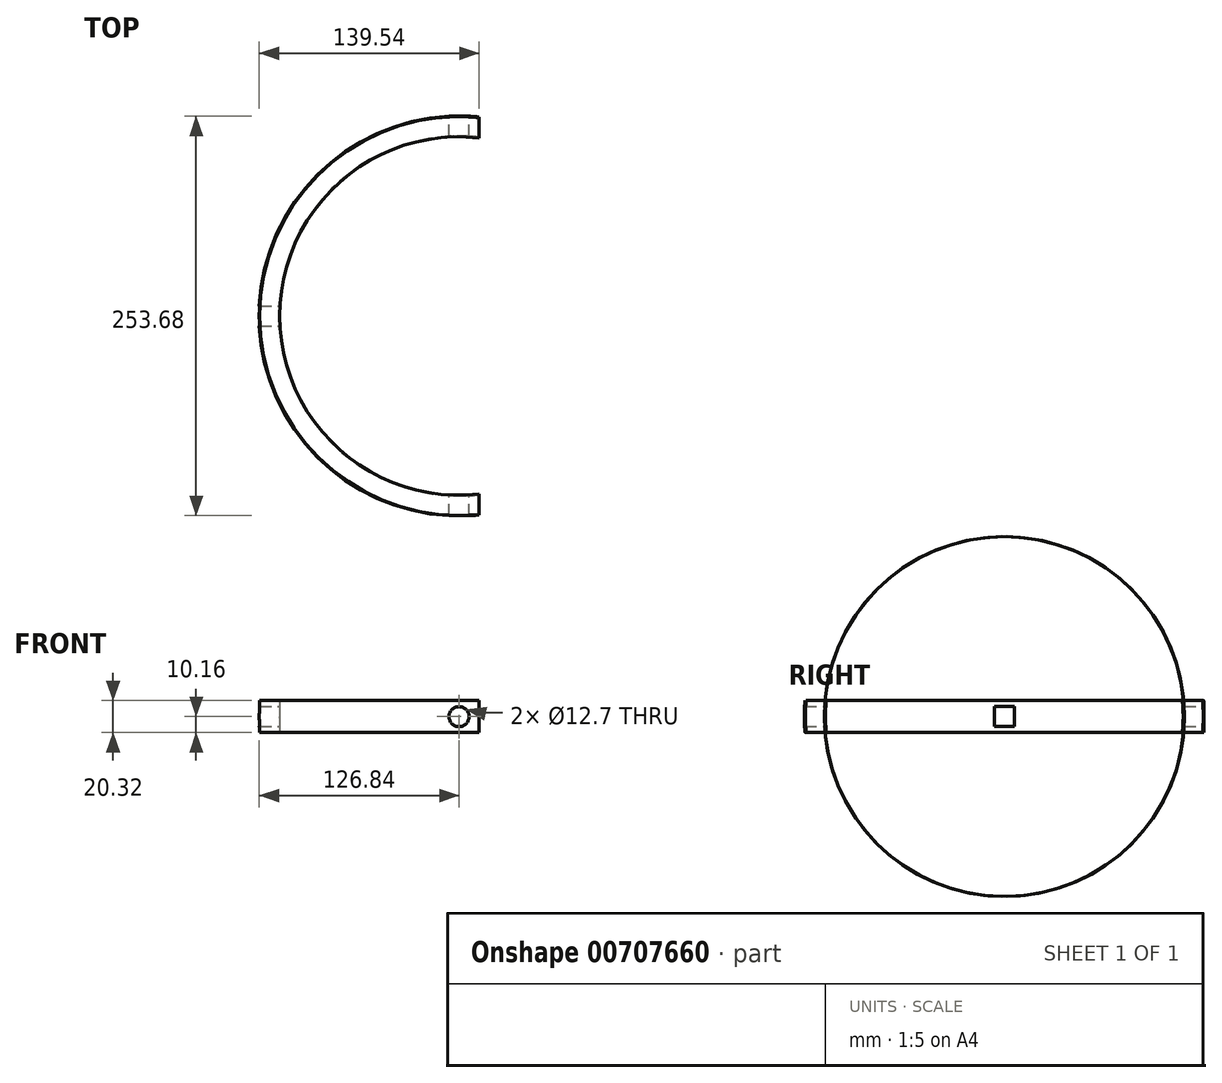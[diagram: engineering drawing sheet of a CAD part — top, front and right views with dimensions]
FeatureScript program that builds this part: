
annotation { "Feature Type Name" : "Feature", "Feature Type Description" : "" }
export const myFeature = defineFeature(function(context is Context, id is Id, definition is map)
    precondition{}
    {
        {
            var Q0;
            Q0=qCreatedBy(makeId("Top.planeOp"),FACE);
            var sketch = newSketch(context, id + "F0", { "sketchPlane" : qUnion([Q0])});
            skArc(sketch, "E0", {"start": v(12.7, 126.36) * mm, "mid": v(-85.2, 94.19) * mm, "end": v(-127, 0) * mm});
            skArc(sketch, "E1", {"start": v(12.7, 113.6) * mm, "mid": v(-76.2, 85.2) * mm, "end": v(-114.3, 0) * mm});
            skLineSegment(sketch, "E2", {"start": v(12.7, 126.36) * mm, "end": v(12.7, 113.6) * mm});
            skLineSegment(sketch, "E3", {"start": v(-127, 0) * mm, "end": v(-114.3, 0) * mm});
            skLineSegment(sketch, "E4", {"start": v(-86.87, 0) * mm, "end": v(85.39, 0) * mm, "construction": true});
            skSolve(sketch);
        }
        {
            var Q0;
            Q0 = qSketchRegion(id + "F0", true);
            var Q1;
            Q1=sQuery(id+"F0.wireOp",EDGE,"E4");
            revolve(context, id + "F1", {"surfaceOperationType" : NewSurfaceOperationType.NEW, "entities" : qUnion([Q0]), "axis" : qUnion([Q1]), "revolveType" : RevolveType.FULL});
        }
        {
            var Q0;
            Q0=qCreatedBy(makeId("Right.planeOp"),FACE);
            var sketch = newSketch(context, id + "F2", { "sketchPlane" : qUnion([Q0])});
            skLineSegment(sketch, "E5.bottom", {"start": v(-6.35, 6.35) * mm, "end": v(6.35, 6.35) * mm});
            skLineSegment(sketch, "E5.top", {"start": v(-6.35, -6.35) * mm, "end": v(6.35, -6.35) * mm});
            skLineSegment(sketch, "E5.left", {"start": v(-6.35, 6.35) * mm, "end": v(-6.35, -6.35) * mm});
            skLineSegment(sketch, "E5.right", {"start": v(6.35, 6.35) * mm, "end": v(6.35, -6.35) * mm});
            skLineSegment(sketch, "E6.bottom", {"start": v(-169.08, 138.73) * mm, "end": v(200.28, 138.73) * mm});
            skLineSegment(sketch, "E6.top", {"start": v(-169.08, 10.16) * mm, "end": v(200.28, 10.16) * mm});
            skLineSegment(sketch, "E6.left", {"start": v(-169.08, 138.73) * mm, "end": v(-169.08, 10.16) * mm});
            skLineSegment(sketch, "E6.right", {"start": v(200.28, 138.73) * mm, "end": v(200.28, 10.16) * mm});
            skLineSegment(sketch, "E7.bottom", {"start": v(-163.02, -10.16) * mm, "end": v(196.26, -10.16) * mm});
            skLineSegment(sketch, "E7.top", {"start": v(-163.02, -153.36) * mm, "end": v(196.26, -153.36) * mm});
            skLineSegment(sketch, "E7.left", {"start": v(-163.02, -10.16) * mm, "end": v(-163.02, -153.36) * mm});
            skLineSegment(sketch, "E7.right", {"start": v(196.26, -10.16) * mm, "end": v(196.26, -153.36) * mm});
            skSolve(sketch);
        }
        {
            var Q0;
            Q0=makeQuery(id+"F2.imprint","IMPRINT",FACE,{"disambiguationData":[TD([[makeQuery(id+"F2.imprint","IMPRINT",EDGE,{"derivedFrom":sQuery(id+"F2.wireOp",EDGE,"E6.bottom")}),-1.0]])]});
            var Q1;
            Q1=makeQuery(id+"F2.imprint","IMPRINT",FACE,{"disambiguationData":[TD([[makeQuery(id+"F2.imprint","IMPRINT",EDGE,{"derivedFrom":sQuery(id+"F2.wireOp",EDGE,"E7.bottom")}),-1.0]])]});
            var Q2;
            Q2=makeQuery(id+"F2.imprint","IMPRINT",FACE,{"disambiguationData":[TD([[makeQuery(id+"F2.imprint","IMPRINT",EDGE,{"derivedFrom":sQuery(id+"F2.wireOp",EDGE,"E5.bottom")}),-1.0]])]});
            extrude(context, id + "F3", {"entities" : qUnion([Q0, Q1, Q2]), "operationType" : NewBodyOperationType.REMOVE, "endBound" : BoundingType.SYMMETRIC, "oppositeDirection" : true, "depth" : 411.48 * mm, "offsetDistance" : 25.4 * mm});
        }
        {
            var Q0;
            Q0=qCreatedBy(makeId("Front.planeOp"),FACE);
            var sketch = newSketch(context, id + "F4", { "sketchPlane" : qUnion([Q0])});
            skCircle(sketch, "E8", {"center": v(0, 0) * mm, "radius": 6.35 * mm});
            skSolve(sketch);
        }
        {
            var Q0;
            Q0 = qSketchRegion(id + "F4", true);
            extrude(context, id + "F5", {"entities" : qUnion([Q0]), "operationType" : NewBodyOperationType.REMOVE, "endBound" : BoundingType.SYMMETRIC, "depth" : 306.83 * mm, "offsetDistance" : 25.4 * mm});
        }
    });
